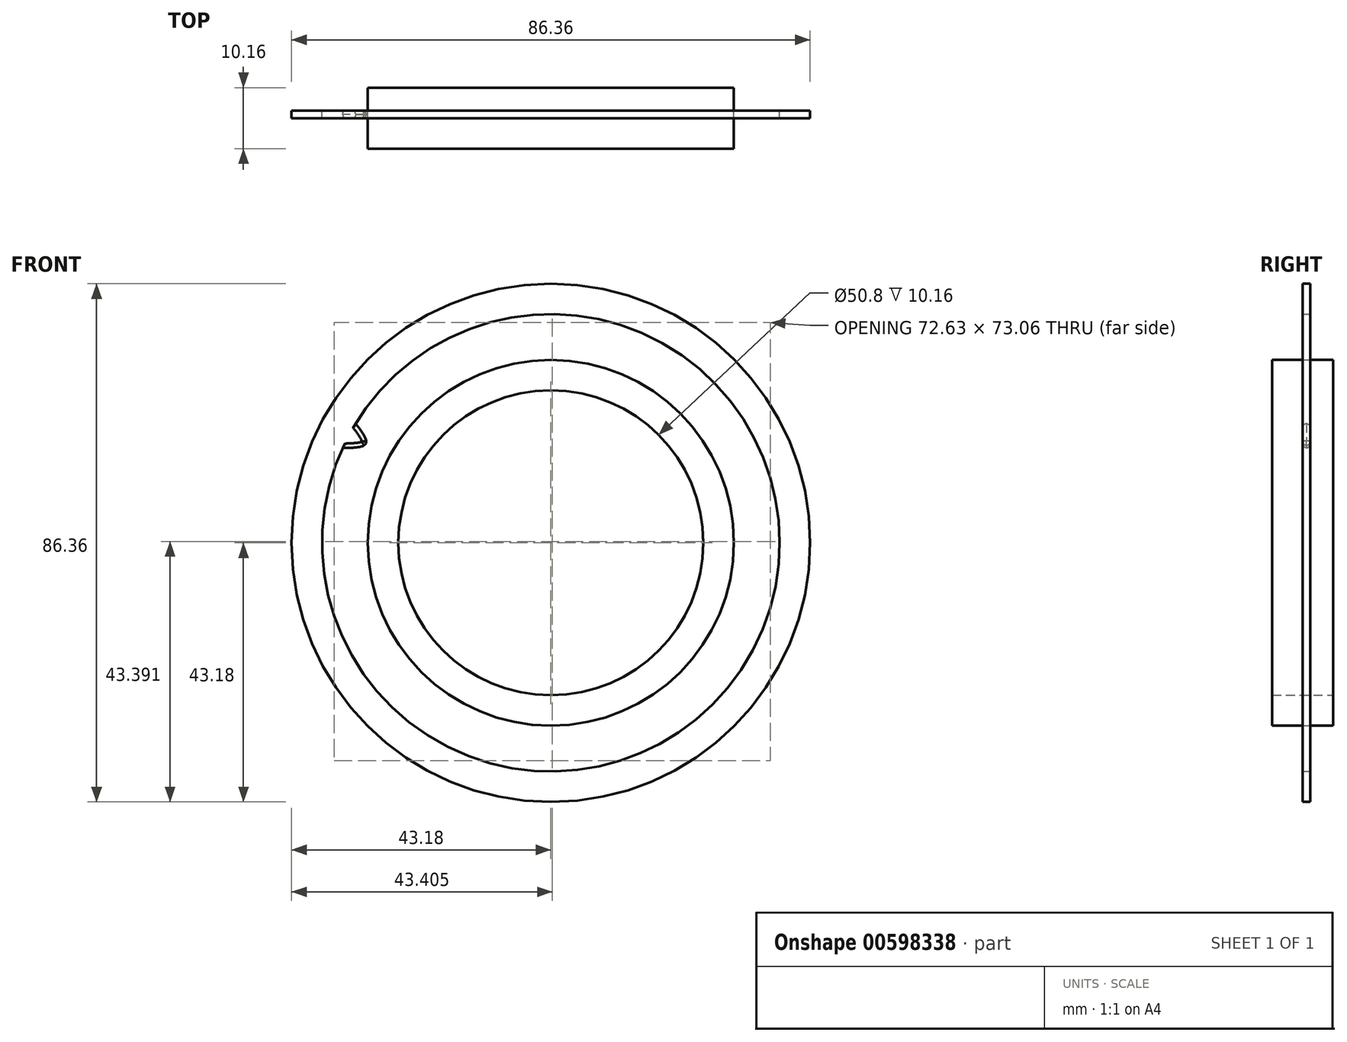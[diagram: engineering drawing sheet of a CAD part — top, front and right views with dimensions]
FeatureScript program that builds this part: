
annotation { "Feature Type Name" : "Feature", "Feature Type Description" : "" }
export const myFeature = defineFeature(function(context is Context, id is Id, definition is map)
    precondition{}
    {
        {
            var Q0;
            Q0=qCreatedBy(makeId("Front.planeOp"),FACE);
            var sketch = newSketch(context, id + "F0", { "sketchPlane" : qUnion([Q0])});
            skCircle(sketch, "E0", {"center": v(0, 0) * mm, "radius": 25.4 * mm});
            skCircle(sketch, "E1.0", {"center": v(0, 0) * mm, "radius": 30.48 * mm});
            skCircle(sketch, "E2.0", {"center": v(0, 0) * mm, "radius": 27.94 * mm});
            skCircle(sketch, "E3.0", {"center": v(0, 0) * mm, "radius": 33.02 * mm});
            skSolve(sketch);
        }
        {
            var Q0;
            Q0=makeQuery(id+"F0.imprint","IMPRINT",FACE,{"disambiguationData":[TD([[makeQuery(id+"F0.imprint","IMPRINT",EDGE,{"derivedFrom":sQuery(id+"F0.wireOp",EDGE,"E2.0")}),-1.0]])]});
            var Q1;
            Q1=makeQuery(id+"F0.imprint","IMPRINT",FACE,{"disambiguationData":[TD([[makeQuery(id+"F0.imprint","IMPRINT",EDGE,{"derivedFrom":sQuery(id+"F0.wireOp",EDGE,"E0")}),-1.0]])]});
            extrude(context, id + "F1", {"entities" : qUnion([Q0, Q1]), "depth" : 10.16 * mm, "offsetDistance" : 25.4 * mm});
        }
        {
            var Q0;
            Q0=qCreatedBy(makeId("Front.planeOp"),FACE);
            cPlane(context, id + "F2", {"entities" : qUnion([Q0]), "cplaneType" : CPlaneType.OFFSET, "offset" : 3.8 * mm, "width" : 152.4 * mm, "height" : 152.4 * mm});
        }
        {
            var Q0;
            Q0=qCreatedBy(id+"F2.planeOp",FACE);
            var sketch = newSketch(context, id + "F3", { "sketchPlane" : qUnion([Q0])});
            skCircle(sketch, "E4.0", {"center": v(0, 0) * mm, "radius": 43.18 * mm});
            skCircle(sketch, "E4.1", {"center": v(0, 0) * mm, "radius": 38.1 * mm});
            skCircle(sketch, "E4.2", {"center": v(0, 0) * mm, "radius": 30.48 * mm});
            skCircle(sketch, "E4.3", {"center": v(0, 0) * mm, "radius": 25.4 * mm});
            skFitSpline(sketch, "E5", {"points": [v(-32.5, 19.88) * mm, v(-30.81, 16.53) * mm, v(-34.68, 15.78) * mm], "startDerivative": vector(6.08, -8.06) * mm, "endDerivative": vector(-10.4, -0.17) * mm});
            skSolve(sketch);
        }
        {
            var Q0;
            Q0 = qSketchRegion(id + "F3", true);
            var Q1;
            {var subQ0=sQuery(id+"F3.wireOp",EDGE,"E5");Q1=makeQuery(id+"F3.imprint","IMPRINT",FACE,{"disambiguationData":[TD([[makeQuery(id+"F3.imprint","IMPRINT",EDGE,{"derivedFrom":subQ0}),-1.0]])]});}
            extrude(context, id + "F4", {"entities" : qUnion([Q0, Q1]), "operationType" : NewBodyOperationType.ADD, "depth" : 1.27 * mm, "offsetDistance" : 25.4 * mm});
        }
        {
            var Q0;
            Q0=makeQuery(id+"F4.opExtrude","CAP_EDGE",EDGE,{"disambiguationData":[OSD([sQuery(id+"F3.wireOp",EDGE,"E5")])],"isStart":false});
            var Q1;
            Q1=makeQuery(id+"F4.opExtrude","CAP_EDGE",EDGE,{"disambiguationData":[OSD([sQuery(id+"F3.wireOp",EDGE,"E5")])],"isStart":true});
            fillet(context, id + "F5", {"entities" : qUnion([Q0, Q1]), "radius" : 0.76 * mm, "tangentPropagation" : true, "allowEdgeOverflow" : false});
        }
    });
